# Revit family: Sanitary_Showers_hansgrohe_13440XXX-hansgrohe-Basic-set-for-4-hole_nnnnnnnnew
name_source: partatom
category: Plumbing Fixtures
revit_build: Autodesk Revit 2015 (Build: 20140903_1530(x64)
units: mm (PartAtom-declared; Revit-internal decimal feet)

## types (1)
- n.a.
    Always visible = Yes
    BIMobject category = Showers
    BIMobject category code = sanitary-showers
    BIMobject main category = Sanitary
    BIMobject main category code = sanitary
    Brand url = http://www.hansgrohe-int.com
    Design country = Germany
    Edition number = 1
    GTIN code = https://4059625321218
    IFC Classification = Sanitary Terminal
    Installation instructions = https://www.hansgrohe.com
    Manufacturer country = Germany
    Manufacturer name = hansgrohe
    Material 1 = Hansgrohe - Hansgrohe - 000 Chrome
    Material 2 = Hansgrohe - Hansgrohe - Brass
    Material 3 = Hansgrohe - Hansgrohe - Beige
    Material 4 = Hansgrohe - Hansgrohe - White
    Material 5 = Hansgrohe - Hansgrohe - Green
    Product Guid = b1579425-f9c4-41c8-a8a1-6b8d5eb0c74e
    Product SKU = 13440XXX
    Product data url = https://bimobject.com
    Product family = hansgrohe
    Product group = Concealed Basic set 3-/4- hole bath mixers
    Product name = 13440XXX hansgrohe Basic set for 4-hole rim mounted bath mixer
    Product url = https://www.hansgrohe.com
    QR code = http://bimobject.com
    Technical description = https://www.hansgrohe.com

## geometry (parser evidence)
native form markers: Sweep x3
no freeform markers — native parametric forms only
